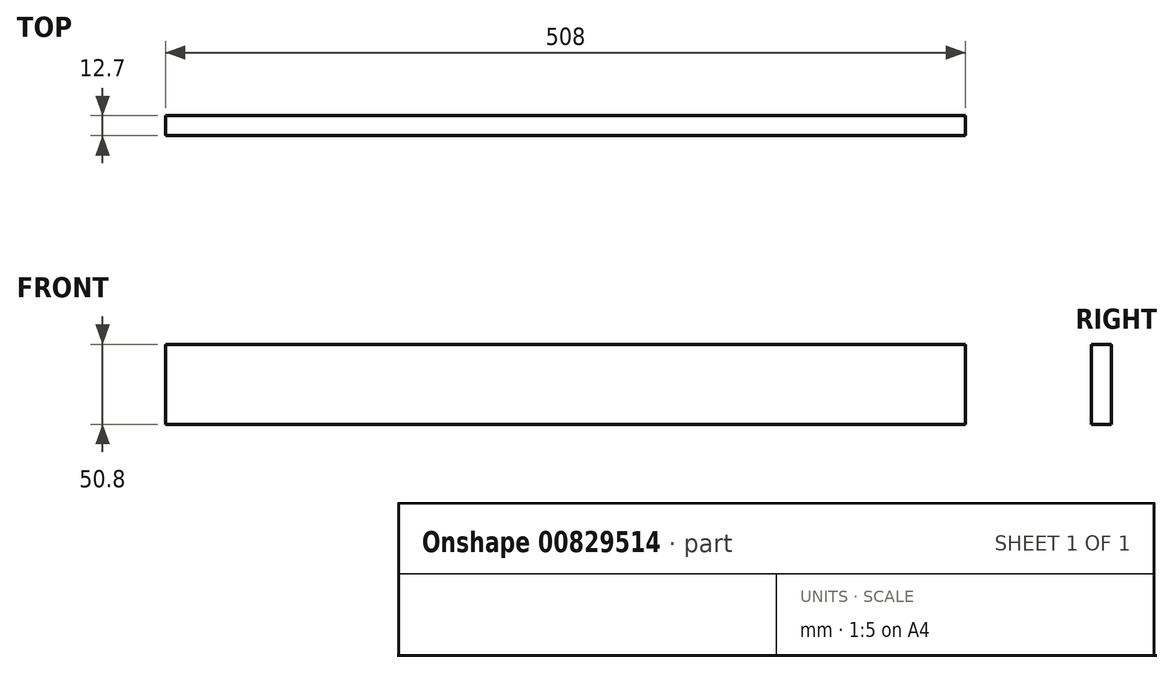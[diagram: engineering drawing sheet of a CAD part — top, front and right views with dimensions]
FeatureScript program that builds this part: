
annotation { "Feature Type Name" : "Feature", "Feature Type Description" : "" }
export const myFeature = defineFeature(function(context is Context, id is Id, definition is map)
    precondition{}
    {
        {
            var Q0;
            Q0=qCreatedBy(makeId("Front.planeOp"),FACE);
            var sketch = newSketch(context, id + "F0", { "sketchPlane" : qUnion([Q0])});
            skLineSegment(sketch, "E0.bottom", {"start": v(-254, -25.4) * mm, "end": v(254, -25.4) * mm});
            skLineSegment(sketch, "E0.top", {"start": v(-254, 25.4) * mm, "end": v(254, 25.4) * mm});
            skLineSegment(sketch, "E0.left", {"start": v(-254, -25.4) * mm, "end": v(-254, 25.4) * mm});
            skLineSegment(sketch, "E0.right", {"start": v(254, -25.4) * mm, "end": v(254, 25.4) * mm});
            skPoint(sketch, "E0.middle", {"position": v(0, 0) * mm});
            skSolve(sketch);
        }
        {
            var Q0;
            Q0 = qSketchRegion(id + "F0", true);
            extrude(context, id + "F1", {"entities" : qUnion([Q0]), "depth" : 12.7 * mm, "offsetDistance" : 25.4 * mm});
        }
    });
